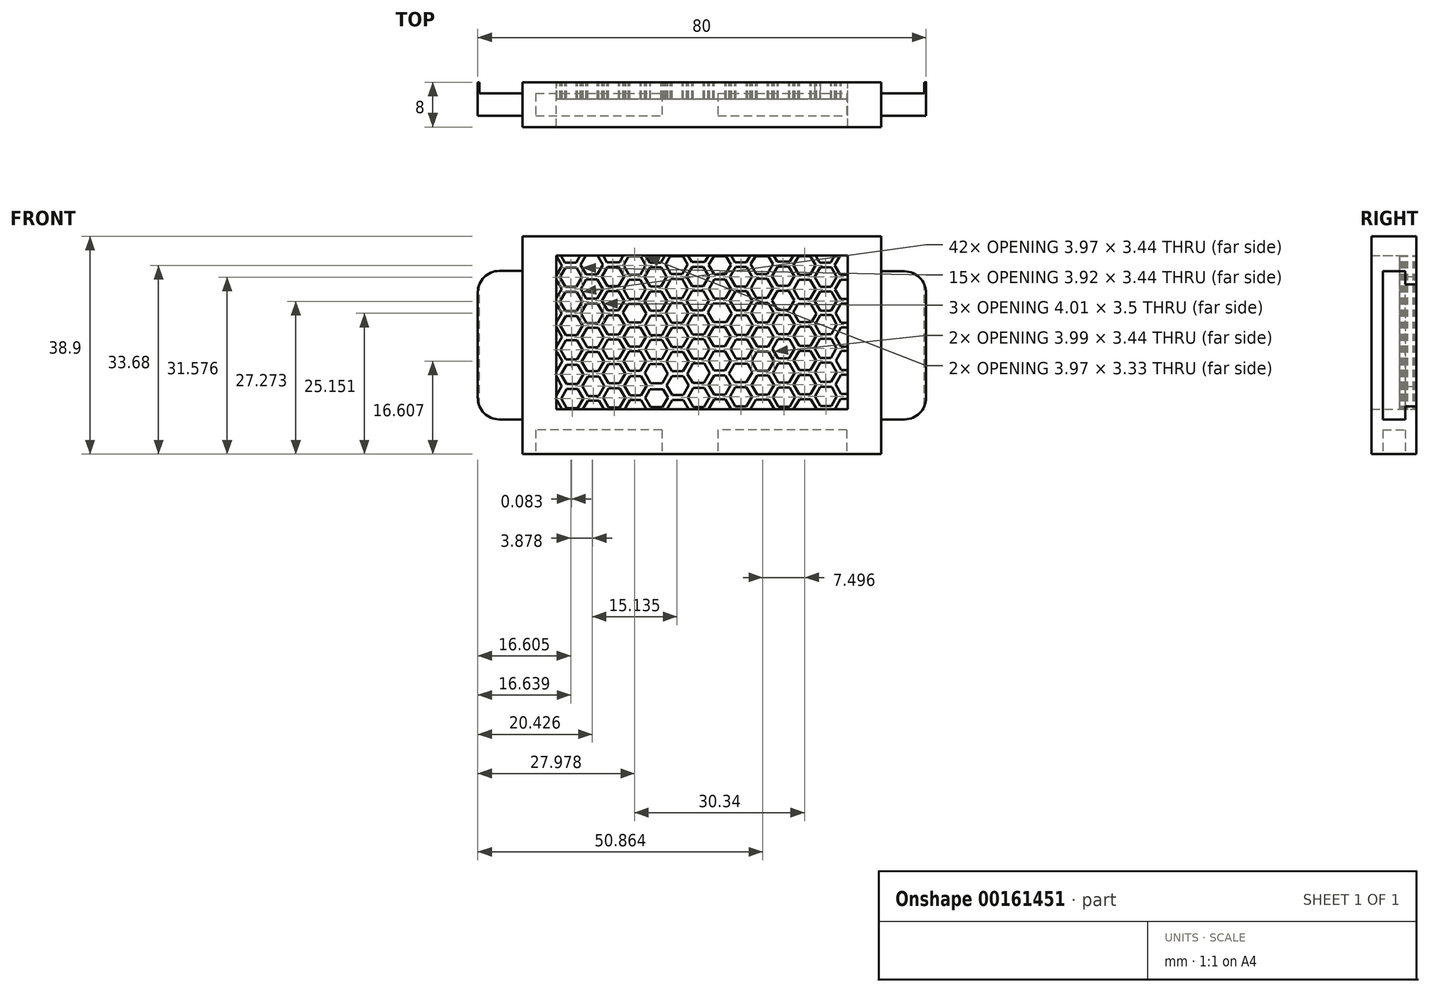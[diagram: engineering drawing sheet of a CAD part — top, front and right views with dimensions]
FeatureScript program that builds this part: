
annotation { "Feature Type Name" : "Feature", "Feature Type Description" : "" }
export const myFeature = defineFeature(function(context is Context, id is Id, definition is map)
    precondition{}
    {
        {
            var Q0;
            Q0=qCreatedBy(makeId("Front.planeOp"),FACE);
            var sketch = newSketch(context, id + "F0", { "sketchPlane" : qUnion([Q0])});
            skLineSegment(sketch, "E0.top", {"start": v(-77.72, 0.67) * mm, "end": v(-71.72, 0.67) * mm});
            skLineSegment(sketch, "E0.left", {"start": v(-77.72, 39.57) * mm, "end": v(-77.72, 0.67) * mm});
            skLineSegment(sketch, "E0.right", {"start": v(-13.72, 39.57) * mm, "end": v(-13.72, 0.67) * mm});
            skLineSegment(sketch, "E1.left", {"start": v(-77.72, 0.67) * mm, "end": v(-77.72, 15.56) * mm});
            skLineSegment(sketch, "E1.right", {"start": v(-85.72, 10.7) * mm, "end": v(-85.72, 29.54) * mm});
            skLineSegment(sketch, "E2.top", {"start": v(-77.72, 6.87) * mm, "end": v(-81.89, 6.87) * mm});
            skLineSegment(sketch, "E2.left", {"start": v(-77.72, 0.67) * mm, "end": v(-77.72, 6.87) * mm});
            skLineSegment(sketch, "E3.top", {"start": v(-81.89, 33.37) * mm, "end": v(-77.72, 33.37) * mm});
            skLineSegment(sketch, "E3.right", {"start": v(-77.72, 33.37) * mm, "end": v(-77.72, 15.56) * mm});
            skArc(sketch, "E4.filletArc", {"start": v(-81.89, 33.37) * mm, "mid": v(-84.6, 32.25) * mm, "end": v(-85.72, 29.54) * mm});
            skPoint(sketch, "E5.visualSharp", {"position": v(-85.72, 6.87) * mm});
            skArc(sketch, "E5.filletArc", {"start": v(-85.72, 10.7) * mm, "mid": v(-84.6, 8) * mm, "end": v(-81.89, 6.87) * mm});
            skLineSegment(sketch, "E6.right", {"start": v(-71.72, 36.1) * mm, "end": v(-71.72, 32.73) * mm});
            skLineSegment(sketch, "E7.top", {"start": v(-13.72, 0.67) * mm, "end": v(-19.72, 0.67) * mm});
            skLineSegment(sketch, "E7.right", {"start": v(-19.72, 36.1) * mm, "end": v(-19.72, 8.67) * mm});
            skLineSegment(sketch, "E8.left", {"start": v(-77.72, 8.67) * mm, "end": v(-77.72, 0.67) * mm});
            skLineSegment(sketch, "E8.right", {"start": v(-13.72, 6.87) * mm, "end": v(-13.72, 0.67) * mm});
            skLineSegment(sketch, "E9.bottom", {"start": v(-36.17, 36.01) * mm, "end": v(-33.87, 36.01) * mm});
            skLineSegment(sketch, "E10.trimOffspring", {"start": v(-43.6, 36.01) * mm, "end": v(-41.43, 36.01) * mm});
            skLineSegment(sketch, "E11.trimOffspring", {"start": v(-28.45, 36.01) * mm, "end": v(-26.35, 36.01) * mm});
            skLineSegment(sketch, "E12", {"start": v(-85.42, 9.22) * mm, "end": v(-85.42, 31.03) * mm});
            skLineSegment(sketch, "E13.0", {"start": v(-64.38, 28.45) * mm, "end": v(-66.36, 28.45) * mm});
            skLineSegment(sketch, "E13.1", {"start": v(-66.36, 28.45) * mm, "end": v(-67.36, 30.17) * mm});
            skLineSegment(sketch, "E13.2", {"start": v(-67.36, 30.17) * mm, "end": v(-66.36, 31.89) * mm});
            skLineSegment(sketch, "E13.3", {"start": v(-66.36, 31.89) * mm, "end": v(-64.38, 31.89) * mm});
            skLineSegment(sketch, "E13.4", {"start": v(-64.38, 31.89) * mm, "end": v(-63.39, 30.17) * mm});
            skLineSegment(sketch, "E13.5", {"start": v(-63.39, 30.17) * mm, "end": v(-64.38, 28.45) * mm});
            skLineSegment(sketch, "E14", {"start": v(-67.15, 32.27) * mm, "end": v(-68.16, 30.53) * mm});
            skLineSegment(sketch, "E15", {"start": v(-66.3, 27.57) * mm, "end": v(-64.3, 27.57) * mm});
            skLineSegment(sketch, "E16.0", {"start": v(-64.39, 32.75) * mm, "end": v(-66.37, 32.75) * mm});
            skLineSegment(sketch, "E16.1", {"start": v(-66.37, 32.75) * mm, "end": v(-67.36, 34.47) * mm});
            skLineSegment(sketch, "E16.2", {"start": v(-67.36, 34.47) * mm, "end": v(-66.43, 36.1) * mm});
            skLineSegment(sketch, "E16.5", {"start": v(-63.4, 34.47) * mm, "end": v(-64.39, 32.75) * mm});
            skLineSegment(sketch, "E17", {"start": v(-67.44, 36.1) * mm, "end": v(-68.17, 34.83) * mm});
            skLineSegment(sketch, "E18.0", {"start": v(-60.6, 26.33) * mm, "end": v(-62.58, 26.33) * mm});
            skLineSegment(sketch, "E18.1", {"start": v(-62.58, 26.33) * mm, "end": v(-63.57, 28.05) * mm});
            skLineSegment(sketch, "E18.2", {"start": v(-63.57, 28.05) * mm, "end": v(-62.58, 29.77) * mm});
            skLineSegment(sketch, "E18.3", {"start": v(-62.58, 29.77) * mm, "end": v(-60.6, 29.77) * mm});
            skLineSegment(sketch, "E18.4", {"start": v(-60.6, 29.77) * mm, "end": v(-59.6, 28.05) * mm});
            skLineSegment(sketch, "E18.5", {"start": v(-59.6, 28.05) * mm, "end": v(-60.6, 26.33) * mm});
            skLineSegment(sketch, "E19", {"start": v(-64.3, 27.57) * mm, "end": v(-63.29, 25.81) * mm});
            skLineSegment(sketch, "E20", {"start": v(-58.91, 27.5) * mm, "end": v(-59.8, 25.94) * mm});
            skLineSegment(sketch, "E21.0", {"start": v(-60.6, 30.63) * mm, "end": v(-62.59, 30.63) * mm});
            skLineSegment(sketch, "E21.1", {"start": v(-62.59, 30.63) * mm, "end": v(-63.58, 32.35) * mm});
            skLineSegment(sketch, "E21.2", {"start": v(-63.58, 32.35) * mm, "end": v(-62.59, 34.07) * mm});
            skLineSegment(sketch, "E21.3", {"start": v(-62.59, 34.07) * mm, "end": v(-60.6, 34.07) * mm});
            skLineSegment(sketch, "E21.4", {"start": v(-60.6, 34.07) * mm, "end": v(-59.6, 32.35) * mm});
            skLineSegment(sketch, "E21.5", {"start": v(-59.6, 32.35) * mm, "end": v(-60.6, 30.63) * mm});
            skLineSegment(sketch, "E22", {"start": v(-60.43, 34.94) * mm, "end": v(-62.66, 34.94) * mm});
            skLineSegment(sketch, "E23.0", {"start": v(-68.09, 26.22) * mm, "end": v(-70.07, 26.22) * mm});
            skLineSegment(sketch, "E23.1", {"start": v(-70.07, 26.22) * mm, "end": v(-71.07, 27.94) * mm});
            skLineSegment(sketch, "E23.2", {"start": v(-71.07, 27.94) * mm, "end": v(-70.07, 29.66) * mm});
            skLineSegment(sketch, "E23.3", {"start": v(-70.07, 29.66) * mm, "end": v(-68.1, 29.66) * mm});
            skLineSegment(sketch, "E23.4", {"start": v(-68.1, 29.66) * mm, "end": v(-67.1, 27.94) * mm});
            skLineSegment(sketch, "E23.5", {"start": v(-67.1, 27.94) * mm, "end": v(-68.09, 26.22) * mm});
            skLineSegment(sketch, "E24", {"start": v(-66.3, 27.57) * mm, "end": v(-67.3, 25.83) * mm});
            skLineSegment(sketch, "E25.0", {"start": v(-68.16, 30.53) * mm, "end": v(-70.08, 30.53) * mm});
            skLineSegment(sketch, "E25.1", {"start": v(-70.08, 30.53) * mm, "end": v(-71.07, 32.25) * mm});
            skLineSegment(sketch, "E25.2", {"start": v(-71.07, 32.25) * mm, "end": v(-70.08, 33.96) * mm});
            skLineSegment(sketch, "E25.3", {"start": v(-70.08, 33.96) * mm, "end": v(-68.1, 33.96) * mm});
            skLineSegment(sketch, "E25.4", {"start": v(-68.1, 33.96) * mm, "end": v(-67.15, 32.27) * mm});
            skLineSegment(sketch, "E26", {"start": v(-68.17, 34.83) * mm, "end": v(-70.16, 34.83) * mm});
            skLineSegment(sketch, "E27.0", {"start": v(-60.5, 17.7) * mm, "end": v(-62.49, 17.7) * mm});
            skLineSegment(sketch, "E27.1", {"start": v(-62.49, 17.7) * mm, "end": v(-63.48, 19.41) * mm});
            skLineSegment(sketch, "E27.2", {"start": v(-63.48, 19.41) * mm, "end": v(-62.49, 21.13) * mm});
            skLineSegment(sketch, "E27.3", {"start": v(-62.49, 21.13) * mm, "end": v(-60.5, 21.13) * mm});
            skLineSegment(sketch, "E27.4", {"start": v(-60.5, 21.13) * mm, "end": v(-59.5, 19.41) * mm});
            skLineSegment(sketch, "E27.5", {"start": v(-59.5, 19.41) * mm, "end": v(-60.5, 17.7) * mm});
            skLineSegment(sketch, "E28", {"start": v(-63.28, 21.51) * mm, "end": v(-64.28, 19.77) * mm});
            skLineSegment(sketch, "E29.0", {"start": v(-60.51, 22) * mm, "end": v(-62.5, 22) * mm});
            skLineSegment(sketch, "E29.1", {"start": v(-62.5, 22) * mm, "end": v(-63.49, 23.71) * mm});
            skLineSegment(sketch, "E29.2", {"start": v(-63.49, 23.71) * mm, "end": v(-62.5, 25.43) * mm});
            skLineSegment(sketch, "E29.3", {"start": v(-62.5, 25.43) * mm, "end": v(-60.51, 25.43) * mm});
            skLineSegment(sketch, "E29.4", {"start": v(-60.51, 25.43) * mm, "end": v(-59.52, 23.71) * mm});
            skLineSegment(sketch, "E29.5", {"start": v(-59.52, 23.71) * mm, "end": v(-60.51, 22) * mm});
            skLineSegment(sketch, "E30", {"start": v(-63.29, 25.81) * mm, "end": v(-64.3, 24.07) * mm});
            skLineSegment(sketch, "E31", {"start": v(-59.8, 25.94) * mm, "end": v(-58.79, 24.18) * mm});
            skLineSegment(sketch, "E32.0", {"start": v(-56.72, 15.57) * mm, "end": v(-58.7, 15.57) * mm});
            skLineSegment(sketch, "E32.1", {"start": v(-58.7, 15.57) * mm, "end": v(-59.7, 17.29) * mm});
            skLineSegment(sketch, "E32.2", {"start": v(-59.7, 17.29) * mm, "end": v(-58.7, 19) * mm});
            skLineSegment(sketch, "E32.3", {"start": v(-58.7, 19) * mm, "end": v(-56.72, 19) * mm});
            skLineSegment(sketch, "E32.4", {"start": v(-56.72, 19) * mm, "end": v(-55.72, 17.29) * mm});
            skLineSegment(sketch, "E32.5", {"start": v(-55.72, 17.29) * mm, "end": v(-56.72, 15.57) * mm});
            skLineSegment(sketch, "E33", {"start": v(-60.38, 16.73) * mm, "end": v(-59.39, 15.01) * mm});
            skLineSegment(sketch, "E34", {"start": v(-55.03, 16.74) * mm, "end": v(-55.92, 15.18) * mm});
            skLineSegment(sketch, "E35.0", {"start": v(-56.72, 19.87) * mm, "end": v(-58.7, 19.87) * mm});
            skLineSegment(sketch, "E35.1", {"start": v(-58.7, 19.87) * mm, "end": v(-59.7, 21.6) * mm});
            skLineSegment(sketch, "E35.2", {"start": v(-59.7, 21.6) * mm, "end": v(-58.7, 23.31) * mm});
            skLineSegment(sketch, "E35.3", {"start": v(-58.7, 23.31) * mm, "end": v(-56.72, 23.31) * mm});
            skLineSegment(sketch, "E35.4", {"start": v(-56.72, 23.31) * mm, "end": v(-55.73, 21.6) * mm});
            skLineSegment(sketch, "E35.5", {"start": v(-55.73, 21.6) * mm, "end": v(-56.72, 19.87) * mm});
            skLineSegment(sketch, "E36", {"start": v(-56.55, 24.18) * mm, "end": v(-58.79, 24.18) * mm});
            skLineSegment(sketch, "E37", {"start": v(-58.7, 19) * mm, "end": v(-56.7, 19) * mm});
            skLineSegment(sketch, "E38.0", {"start": v(-68, 17.59) * mm, "end": v(-69.98, 17.59) * mm});
            skLineSegment(sketch, "E38.1", {"start": v(-69.98, 17.59) * mm, "end": v(-70.97, 19.3) * mm});
            skLineSegment(sketch, "E38.2", {"start": v(-70.97, 19.3) * mm, "end": v(-69.98, 21.02) * mm});
            skLineSegment(sketch, "E38.3", {"start": v(-69.98, 21.02) * mm, "end": v(-68, 21.02) * mm});
            skLineSegment(sketch, "E38.4", {"start": v(-68, 21.02) * mm, "end": v(-67, 19.3) * mm});
            skLineSegment(sketch, "E38.5", {"start": v(-67, 19.3) * mm, "end": v(-68, 17.59) * mm});
            skLineSegment(sketch, "E39.0", {"start": v(-68, 21.89) * mm, "end": v(-70, 21.89) * mm});
            skLineSegment(sketch, "E39.1", {"start": v(-70, 21.89) * mm, "end": v(-70.98, 23.6) * mm});
            skLineSegment(sketch, "E39.2", {"start": v(-70.98, 23.6) * mm, "end": v(-70, 25.33) * mm});
            skLineSegment(sketch, "E39.3", {"start": v(-70, 25.33) * mm, "end": v(-68, 25.33) * mm});
            skLineSegment(sketch, "E39.4", {"start": v(-68, 25.33) * mm, "end": v(-67.01, 23.6) * mm});
            skLineSegment(sketch, "E39.5", {"start": v(-67.01, 23.6) * mm, "end": v(-68, 21.89) * mm});
            skLineSegment(sketch, "E40", {"start": v(-67.3, 25.83) * mm, "end": v(-66.28, 24.07) * mm});
            skLineSegment(sketch, "E41.0", {"start": v(-64.21, 15.46) * mm, "end": v(-66.2, 15.46) * mm});
            skLineSegment(sketch, "E41.1", {"start": v(-66.2, 15.46) * mm, "end": v(-67.19, 17.18) * mm});
            skLineSegment(sketch, "E41.2", {"start": v(-67.19, 17.18) * mm, "end": v(-66.2, 18.9) * mm});
            skLineSegment(sketch, "E41.3", {"start": v(-66.2, 18.9) * mm, "end": v(-64.21, 18.9) * mm});
            skLineSegment(sketch, "E41.4", {"start": v(-64.21, 18.9) * mm, "end": v(-63.22, 17.18) * mm});
            skLineSegment(sketch, "E41.5", {"start": v(-63.22, 17.18) * mm, "end": v(-64.21, 15.46) * mm});
            skLineSegment(sketch, "E42.0", {"start": v(-64.28, 19.77) * mm, "end": v(-66.2, 19.77) * mm});
            skLineSegment(sketch, "E42.1", {"start": v(-66.2, 19.77) * mm, "end": v(-67.2, 21.49) * mm});
            skLineSegment(sketch, "E42.2", {"start": v(-67.2, 21.49) * mm, "end": v(-66.2, 23.2) * mm});
            skLineSegment(sketch, "E42.3", {"start": v(-66.2, 23.2) * mm, "end": v(-64.22, 23.2) * mm});
            skLineSegment(sketch, "E42.4", {"start": v(-64.22, 23.2) * mm, "end": v(-63.28, 21.51) * mm});
            skLineSegment(sketch, "E43", {"start": v(-64.3, 24.07) * mm, "end": v(-66.28, 24.07) * mm});
            skLineSegment(sketch, "E44.0", {"start": v(-49.24, 28.49) * mm, "end": v(-51.23, 28.49) * mm});
            skLineSegment(sketch, "E44.1", {"start": v(-51.23, 28.49) * mm, "end": v(-52.22, 30.2) * mm});
            skLineSegment(sketch, "E44.2", {"start": v(-52.22, 30.2) * mm, "end": v(-51.23, 31.93) * mm});
            skLineSegment(sketch, "E44.3", {"start": v(-51.23, 31.93) * mm, "end": v(-49.25, 31.93) * mm});
            skLineSegment(sketch, "E44.4", {"start": v(-49.25, 31.93) * mm, "end": v(-48.25, 30.2) * mm});
            skLineSegment(sketch, "E44.5", {"start": v(-48.25, 30.2) * mm, "end": v(-49.24, 28.49) * mm});
            skLineSegment(sketch, "E45", {"start": v(-52.02, 32.31) * mm, "end": v(-53.03, 30.57) * mm});
            skLineSegment(sketch, "E46", {"start": v(-51.17, 27.6) * mm, "end": v(-49.17, 27.6) * mm});
            skLineSegment(sketch, "E47.0", {"start": v(-49.25, 32.8) * mm, "end": v(-51.24, 32.8) * mm});
            skLineSegment(sketch, "E47.1", {"start": v(-51.24, 32.8) * mm, "end": v(-52.23, 34.51) * mm});
            skLineSegment(sketch, "E47.2", {"start": v(-52.23, 34.51) * mm, "end": v(-51.36, 36.01) * mm});
            skLineSegment(sketch, "E47.4", {"start": v(-49.13, 36.01) * mm, "end": v(-48.26, 34.51) * mm});
            skLineSegment(sketch, "E47.5", {"start": v(-48.26, 34.51) * mm, "end": v(-49.25, 32.8) * mm});
            skLineSegment(sketch, "E48", {"start": v(-52.38, 36.01) * mm, "end": v(-53.04, 34.87) * mm});
            skLineSegment(sketch, "E49", {"start": v(-48.13, 36.01) * mm, "end": v(-47.53, 34.97) * mm});
            skLineSegment(sketch, "E50.0", {"start": v(-45.46, 26.37) * mm, "end": v(-47.44, 26.37) * mm});
            skLineSegment(sketch, "E50.1", {"start": v(-47.44, 26.37) * mm, "end": v(-48.43, 28.09) * mm});
            skLineSegment(sketch, "E50.2", {"start": v(-48.43, 28.09) * mm, "end": v(-47.44, 29.8) * mm});
            skLineSegment(sketch, "E50.3", {"start": v(-47.44, 29.8) * mm, "end": v(-45.46, 29.8) * mm});
            skLineSegment(sketch, "E50.4", {"start": v(-45.46, 29.8) * mm, "end": v(-44.47, 28.09) * mm});
            skLineSegment(sketch, "E50.5", {"start": v(-44.47, 28.09) * mm, "end": v(-45.46, 26.37) * mm});
            skLineSegment(sketch, "E51", {"start": v(-49.17, 27.6) * mm, "end": v(-48.15, 25.85) * mm});
            skLineSegment(sketch, "E52", {"start": v(-43.77, 27.56) * mm, "end": v(-44.67, 25.98) * mm});
            skLineSegment(sketch, "E53.0", {"start": v(-45.47, 30.67) * mm, "end": v(-47.45, 30.67) * mm});
            skLineSegment(sketch, "E53.1", {"start": v(-47.45, 30.67) * mm, "end": v(-48.44, 32.4) * mm});
            skLineSegment(sketch, "E53.2", {"start": v(-48.44, 32.4) * mm, "end": v(-47.45, 34.1) * mm});
            skLineSegment(sketch, "E53.3", {"start": v(-47.45, 34.1) * mm, "end": v(-45.47, 34.1) * mm});
            skLineSegment(sketch, "E53.4", {"start": v(-45.47, 34.1) * mm, "end": v(-44.47, 32.4) * mm});
            skLineSegment(sketch, "E53.5", {"start": v(-44.47, 32.4) * mm, "end": v(-45.47, 30.67) * mm});
            skLineSegment(sketch, "E54", {"start": v(-45.22, 34.97) * mm, "end": v(-47.53, 34.97) * mm});
            skLineSegment(sketch, "E55", {"start": v(-47.45, 29.8) * mm, "end": v(-45.45, 29.8) * mm});
            skLineSegment(sketch, "E56.0", {"start": v(-56.74, 28.38) * mm, "end": v(-58.73, 28.38) * mm});
            skLineSegment(sketch, "E56.1", {"start": v(-58.73, 28.38) * mm, "end": v(-59.72, 30.1) * mm});
            skLineSegment(sketch, "E56.2", {"start": v(-59.72, 30.1) * mm, "end": v(-58.73, 31.82) * mm});
            skLineSegment(sketch, "E56.3", {"start": v(-58.73, 31.82) * mm, "end": v(-56.74, 31.82) * mm});
            skLineSegment(sketch, "E56.4", {"start": v(-56.74, 31.82) * mm, "end": v(-55.75, 30.1) * mm});
            skLineSegment(sketch, "E56.5", {"start": v(-55.75, 30.1) * mm, "end": v(-56.74, 28.38) * mm});
            skLineSegment(sketch, "E57", {"start": v(-58.91, 27.5) * mm, "end": v(-56.67, 27.5) * mm});
            skLineSegment(sketch, "E58.0", {"start": v(-56.75, 32.69) * mm, "end": v(-58.73, 32.69) * mm});
            skLineSegment(sketch, "E58.1", {"start": v(-58.73, 32.69) * mm, "end": v(-59.73, 34.4) * mm});
            skLineSegment(sketch, "E58.2", {"start": v(-59.73, 34.4) * mm, "end": v(-58.8, 36.01) * mm});
            skLineSegment(sketch, "E58.4", {"start": v(-56.69, 36.01) * mm, "end": v(-55.76, 34.4) * mm});
            skLineSegment(sketch, "E58.5", {"start": v(-55.76, 34.4) * mm, "end": v(-56.75, 32.69) * mm});
            skLineSegment(sketch, "E59", {"start": v(-59.81, 36.01) * mm, "end": v(-60.43, 34.94) * mm});
            skLineSegment(sketch, "E60", {"start": v(-55.69, 36.01) * mm, "end": v(-55.02, 34.87) * mm});
            skLineSegment(sketch, "E61.0", {"start": v(-52.95, 26.26) * mm, "end": v(-54.94, 26.26) * mm});
            skLineSegment(sketch, "E61.1", {"start": v(-54.94, 26.26) * mm, "end": v(-55.93, 27.98) * mm});
            skLineSegment(sketch, "E61.2", {"start": v(-55.93, 27.98) * mm, "end": v(-54.94, 29.7) * mm});
            skLineSegment(sketch, "E61.3", {"start": v(-54.94, 29.7) * mm, "end": v(-52.96, 29.7) * mm});
            skLineSegment(sketch, "E61.4", {"start": v(-52.96, 29.7) * mm, "end": v(-51.96, 27.98) * mm});
            skLineSegment(sketch, "E61.5", {"start": v(-51.96, 27.98) * mm, "end": v(-52.95, 26.26) * mm});
            skLineSegment(sketch, "E62", {"start": v(-56.67, 27.5) * mm, "end": v(-55.65, 25.74) * mm});
            skLineSegment(sketch, "E63", {"start": v(-51.17, 27.6) * mm, "end": v(-52.16, 25.87) * mm});
            skLineSegment(sketch, "E64.0", {"start": v(-53.03, 30.57) * mm, "end": v(-54.95, 30.57) * mm});
            skLineSegment(sketch, "E64.1", {"start": v(-54.95, 30.57) * mm, "end": v(-55.94, 32.28) * mm});
            skLineSegment(sketch, "E64.2", {"start": v(-55.94, 32.28) * mm, "end": v(-54.95, 34) * mm});
            skLineSegment(sketch, "E64.3", {"start": v(-54.95, 34) * mm, "end": v(-52.96, 34) * mm});
            skLineSegment(sketch, "E64.4", {"start": v(-52.96, 34) * mm, "end": v(-52.02, 32.31) * mm});
            skLineSegment(sketch, "E65", {"start": v(-53.04, 34.87) * mm, "end": v(-55.02, 34.87) * mm});
            skLineSegment(sketch, "E66", {"start": v(-54.95, 29.69) * mm, "end": v(-52.95, 29.69) * mm});
            skLineSegment(sketch, "E67.0", {"start": v(-45.37, 17.73) * mm, "end": v(-47.35, 17.73) * mm});
            skLineSegment(sketch, "E67.1", {"start": v(-47.35, 17.73) * mm, "end": v(-48.34, 19.45) * mm});
            skLineSegment(sketch, "E67.2", {"start": v(-48.34, 19.45) * mm, "end": v(-47.35, 21.17) * mm});
            skLineSegment(sketch, "E67.3", {"start": v(-47.35, 21.17) * mm, "end": v(-45.37, 21.17) * mm});
            skLineSegment(sketch, "E67.4", {"start": v(-45.37, 21.17) * mm, "end": v(-44.37, 19.45) * mm});
            skLineSegment(sketch, "E67.5", {"start": v(-44.37, 19.45) * mm, "end": v(-45.37, 17.73) * mm});
            skLineSegment(sketch, "E68", {"start": v(-48.14, 21.55) * mm, "end": v(-49.15, 19.8) * mm});
            skLineSegment(sketch, "E69", {"start": v(-47.3, 16.85) * mm, "end": v(-45.3, 16.85) * mm});
            skLineSegment(sketch, "E70.0", {"start": v(-45.38, 22.03) * mm, "end": v(-47.36, 22.03) * mm});
            skLineSegment(sketch, "E70.1", {"start": v(-47.36, 22.03) * mm, "end": v(-48.35, 23.75) * mm});
            skLineSegment(sketch, "E70.2", {"start": v(-48.35, 23.75) * mm, "end": v(-47.36, 25.47) * mm});
            skLineSegment(sketch, "E70.3", {"start": v(-47.36, 25.47) * mm, "end": v(-45.38, 25.47) * mm});
            skLineSegment(sketch, "E70.4", {"start": v(-45.38, 25.47) * mm, "end": v(-44.38, 23.75) * mm});
            skLineSegment(sketch, "E70.5", {"start": v(-44.38, 23.75) * mm, "end": v(-45.38, 22.03) * mm});
            skLineSegment(sketch, "E71", {"start": v(-48.15, 25.85) * mm, "end": v(-49.16, 24.1) * mm});
            skLineSegment(sketch, "E72", {"start": v(-44.67, 25.98) * mm, "end": v(-43.65, 24.22) * mm});
            skLineSegment(sketch, "E73.0", {"start": v(-41.58, 15.6) * mm, "end": v(-43.56, 15.6) * mm});
            skLineSegment(sketch, "E73.1", {"start": v(-43.56, 15.6) * mm, "end": v(-44.56, 17.33) * mm});
            skLineSegment(sketch, "E73.2", {"start": v(-44.56, 17.33) * mm, "end": v(-43.57, 19.05) * mm});
            skLineSegment(sketch, "E73.3", {"start": v(-43.57, 19.05) * mm, "end": v(-41.58, 19.05) * mm});
            skLineSegment(sketch, "E73.4", {"start": v(-41.58, 19.05) * mm, "end": v(-40.59, 17.33) * mm});
            skLineSegment(sketch, "E73.5", {"start": v(-40.59, 17.33) * mm, "end": v(-41.58, 15.6) * mm});
            skLineSegment(sketch, "E74", {"start": v(-45.3, 16.85) * mm, "end": v(-44.32, 15.16) * mm});
            skLineSegment(sketch, "E75", {"start": v(-39.89, 16.8) * mm, "end": v(-40.88, 15.05) * mm});
            skLineSegment(sketch, "E76.0", {"start": v(-41.59, 19.91) * mm, "end": v(-43.57, 19.91) * mm});
            skLineSegment(sketch, "E76.1", {"start": v(-43.57, 19.91) * mm, "end": v(-44.57, 21.63) * mm});
            skLineSegment(sketch, "E76.2", {"start": v(-44.57, 21.63) * mm, "end": v(-43.57, 23.35) * mm});
            skLineSegment(sketch, "E76.3", {"start": v(-43.57, 23.35) * mm, "end": v(-41.59, 23.35) * mm});
            skLineSegment(sketch, "E76.4", {"start": v(-41.59, 23.35) * mm, "end": v(-40.6, 21.63) * mm});
            skLineSegment(sketch, "E76.5", {"start": v(-40.6, 21.63) * mm, "end": v(-41.59, 19.91) * mm});
            skLineSegment(sketch, "E77", {"start": v(-41.34, 24.22) * mm, "end": v(-43.65, 24.22) * mm});
            skLineSegment(sketch, "E78.0", {"start": v(-52.86, 17.62) * mm, "end": v(-54.85, 17.62) * mm});
            skLineSegment(sketch, "E78.1", {"start": v(-54.85, 17.62) * mm, "end": v(-55.84, 19.34) * mm});
            skLineSegment(sketch, "E78.2", {"start": v(-55.84, 19.34) * mm, "end": v(-54.85, 21.06) * mm});
            skLineSegment(sketch, "E78.3", {"start": v(-54.85, 21.06) * mm, "end": v(-52.86, 21.06) * mm});
            skLineSegment(sketch, "E78.4", {"start": v(-52.86, 21.06) * mm, "end": v(-51.87, 19.34) * mm});
            skLineSegment(sketch, "E78.5", {"start": v(-51.87, 19.34) * mm, "end": v(-52.86, 17.62) * mm});
            skLineSegment(sketch, "E79", {"start": v(-55.03, 16.74) * mm, "end": v(-52.79, 16.74) * mm});
            skLineSegment(sketch, "E80.0", {"start": v(-52.87, 21.93) * mm, "end": v(-54.86, 21.93) * mm});
            skLineSegment(sketch, "E80.1", {"start": v(-54.86, 21.93) * mm, "end": v(-55.85, 23.64) * mm});
            skLineSegment(sketch, "E80.2", {"start": v(-55.85, 23.64) * mm, "end": v(-54.86, 25.36) * mm});
            skLineSegment(sketch, "E80.3", {"start": v(-54.86, 25.36) * mm, "end": v(-52.87, 25.36) * mm});
            skLineSegment(sketch, "E80.4", {"start": v(-52.87, 25.36) * mm, "end": v(-51.88, 23.64) * mm});
            skLineSegment(sketch, "E80.5", {"start": v(-51.88, 23.64) * mm, "end": v(-52.87, 21.93) * mm});
            skLineSegment(sketch, "E81", {"start": v(-55.65, 25.74) * mm, "end": v(-56.55, 24.18) * mm});
            skLineSegment(sketch, "E82", {"start": v(-52.16, 25.87) * mm, "end": v(-51.15, 24.1) * mm});
            skLineSegment(sketch, "E83.0", {"start": v(-49.08, 15.5) * mm, "end": v(-51.06, 15.5) * mm});
            skLineSegment(sketch, "E83.1", {"start": v(-51.06, 15.5) * mm, "end": v(-52.05, 17.22) * mm});
            skLineSegment(sketch, "E83.2", {"start": v(-52.05, 17.22) * mm, "end": v(-51.06, 18.94) * mm});
            skLineSegment(sketch, "E83.3", {"start": v(-51.06, 18.94) * mm, "end": v(-49.08, 18.94) * mm});
            skLineSegment(sketch, "E83.4", {"start": v(-49.08, 18.94) * mm, "end": v(-48.08, 17.22) * mm});
            skLineSegment(sketch, "E83.5", {"start": v(-48.08, 17.22) * mm, "end": v(-49.08, 15.5) * mm});
            skLineSegment(sketch, "E84", {"start": v(-52.79, 16.74) * mm, "end": v(-51.81, 15.05) * mm});
            skLineSegment(sketch, "E85", {"start": v(-51.05, 14.62) * mm, "end": v(-49.04, 14.62) * mm});
            skLineSegment(sketch, "E86", {"start": v(-47.3, 16.85) * mm, "end": v(-48.36, 14.99) * mm});
            skLineSegment(sketch, "E87.0", {"start": v(-49.15, 19.8) * mm, "end": v(-51.07, 19.8) * mm});
            skLineSegment(sketch, "E87.1", {"start": v(-51.07, 19.8) * mm, "end": v(-52.06, 21.52) * mm});
            skLineSegment(sketch, "E87.2", {"start": v(-52.06, 21.52) * mm, "end": v(-51.07, 23.24) * mm});
            skLineSegment(sketch, "E87.3", {"start": v(-51.07, 23.24) * mm, "end": v(-49.09, 23.24) * mm});
            skLineSegment(sketch, "E87.4", {"start": v(-49.09, 23.24) * mm, "end": v(-48.14, 21.55) * mm});
            skLineSegment(sketch, "E88", {"start": v(-49.16, 24.1) * mm, "end": v(-51.15, 24.1) * mm});
            skLineSegment(sketch, "E89.0", {"start": v(-60.37, 9) * mm, "end": v(-62.36, 9) * mm});
            skLineSegment(sketch, "E89.1", {"start": v(-62.36, 9) * mm, "end": v(-63.35, 10.71) * mm});
            skLineSegment(sketch, "E89.2", {"start": v(-63.35, 10.71) * mm, "end": v(-62.36, 12.43) * mm});
            skLineSegment(sketch, "E89.3", {"start": v(-62.36, 12.43) * mm, "end": v(-60.37, 12.43) * mm});
            skLineSegment(sketch, "E89.4", {"start": v(-60.37, 12.43) * mm, "end": v(-59.38, 10.71) * mm});
            skLineSegment(sketch, "E89.5", {"start": v(-59.38, 10.71) * mm, "end": v(-60.37, 9) * mm});
            skLineSegment(sketch, "E90", {"start": v(-63.15, 12.82) * mm, "end": v(-64.16, 11.07) * mm});
            skLineSegment(sketch, "E91.0", {"start": v(-60.38, 13.3) * mm, "end": v(-62.37, 13.3) * mm});
            skLineSegment(sketch, "E91.1", {"start": v(-62.37, 13.3) * mm, "end": v(-63.36, 15.01) * mm});
            skLineSegment(sketch, "E91.2", {"start": v(-63.36, 15.01) * mm, "end": v(-62.37, 16.73) * mm});
            skLineSegment(sketch, "E91.3", {"start": v(-62.37, 16.73) * mm, "end": v(-60.38, 16.73) * mm});
            skLineSegment(sketch, "E91.5", {"start": v(-59.39, 15.01) * mm, "end": v(-60.38, 13.3) * mm});
            skLineSegment(sketch, "E92.2", {"start": v(-59.24, 9.15) * mm, "end": v(-58.57, 10.3) * mm});
            skLineSegment(sketch, "E92.3", {"start": v(-58.57, 10.3) * mm, "end": v(-56.59, 10.3) * mm});
            skLineSegment(sketch, "E92.4", {"start": v(-56.59, 10.3) * mm, "end": v(-55.67, 8.67) * mm});
            skLineSegment(sketch, "E93", {"start": v(-55.83, 10.73) * mm, "end": v(-54.88, 9.04) * mm});
            skLineSegment(sketch, "E94.0", {"start": v(-56.6, 11.18) * mm, "end": v(-58.58, 11.18) * mm});
            skLineSegment(sketch, "E94.1", {"start": v(-58.58, 11.18) * mm, "end": v(-59.57, 12.9) * mm});
            skLineSegment(sketch, "E94.2", {"start": v(-59.57, 12.9) * mm, "end": v(-58.58, 14.61) * mm});
            skLineSegment(sketch, "E94.3", {"start": v(-58.58, 14.61) * mm, "end": v(-56.6, 14.61) * mm});
            skLineSegment(sketch, "E94.4", {"start": v(-56.6, 14.61) * mm, "end": v(-55.6, 12.9) * mm});
            skLineSegment(sketch, "E94.5", {"start": v(-55.6, 12.9) * mm, "end": v(-56.6, 11.18) * mm});
            skLineSegment(sketch, "E95", {"start": v(-55.92, 15.18) * mm, "end": v(-54.87, 13.35) * mm});
            skLineSegment(sketch, "E96", {"start": v(-54.98, 12.22) * mm, "end": v(-55.83, 10.73) * mm});
            skLineSegment(sketch, "E97.0", {"start": v(-67.87, 8.89) * mm, "end": v(-69.85, 8.89) * mm});
            skLineSegment(sketch, "E97.1", {"start": v(-69.85, 8.89) * mm, "end": v(-70.85, 10.6) * mm});
            skLineSegment(sketch, "E97.2", {"start": v(-70.85, 10.6) * mm, "end": v(-69.85, 12.32) * mm});
            skLineSegment(sketch, "E97.3", {"start": v(-69.85, 12.32) * mm, "end": v(-67.87, 12.32) * mm});
            skLineSegment(sketch, "E97.4", {"start": v(-67.87, 12.32) * mm, "end": v(-66.88, 10.6) * mm});
            skLineSegment(sketch, "E97.5", {"start": v(-66.88, 10.6) * mm, "end": v(-67.87, 8.89) * mm});
            skLineSegment(sketch, "E98.0", {"start": v(-67.88, 13.19) * mm, "end": v(-69.86, 13.19) * mm});
            skLineSegment(sketch, "E98.1", {"start": v(-69.86, 13.19) * mm, "end": v(-70.85, 14.9) * mm});
            skLineSegment(sketch, "E98.2", {"start": v(-70.85, 14.9) * mm, "end": v(-69.86, 16.63) * mm});
            skLineSegment(sketch, "E98.3", {"start": v(-69.86, 16.63) * mm, "end": v(-67.88, 16.63) * mm});
            skLineSegment(sketch, "E98.4", {"start": v(-67.88, 16.63) * mm, "end": v(-66.89, 14.9) * mm});
            skLineSegment(sketch, "E98.5", {"start": v(-66.89, 14.9) * mm, "end": v(-67.88, 13.19) * mm});
            skLineSegment(sketch, "E99", {"start": v(-69.86, 12.31) * mm, "end": v(-67.86, 12.31) * mm});
            skLineSegment(sketch, "E100.3", {"start": v(-66.07, 10.2) * mm, "end": v(-64.08, 10.2) * mm});
            skLineSegment(sketch, "E100.4", {"start": v(-64.08, 10.2) * mm, "end": v(-63.22, 8.7) * mm});
            skLineSegment(sketch, "E101.0", {"start": v(-64.16, 11.07) * mm, "end": v(-66.08, 11.07) * mm});
            skLineSegment(sketch, "E101.1", {"start": v(-66.08, 11.07) * mm, "end": v(-67.07, 12.79) * mm});
            skLineSegment(sketch, "E101.2", {"start": v(-67.07, 12.79) * mm, "end": v(-66.08, 14.5) * mm});
            skLineSegment(sketch, "E101.3", {"start": v(-66.08, 14.5) * mm, "end": v(-64.1, 14.5) * mm});
            skLineSegment(sketch, "E101.4", {"start": v(-64.1, 14.5) * mm, "end": v(-63.15, 12.82) * mm});
            skLineSegment(sketch, "E102.1", {"start": v(-44.5, 8.67) * mm, "end": v(-44.52, 8.73) * mm});
            skLineSegment(sketch, "E102.2", {"start": v(-44.52, 8.73) * mm, "end": v(-43.53, 10.45) * mm});
            skLineSegment(sketch, "E102.3", {"start": v(-43.53, 10.45) * mm, "end": v(-41.55, 10.45) * mm});
            skLineSegment(sketch, "E102.4", {"start": v(-41.55, 10.45) * mm, "end": v(-40.55, 8.73) * mm});
            skLineSegment(sketch, "E103", {"start": v(-44.32, 10.83) * mm, "end": v(-45.33, 9.09) * mm});
            skLineSegment(sketch, "E104.0", {"start": v(-41.56, 11.31) * mm, "end": v(-43.54, 11.31) * mm});
            skLineSegment(sketch, "E104.1", {"start": v(-43.54, 11.31) * mm, "end": v(-44.53, 13.03) * mm});
            skLineSegment(sketch, "E104.2", {"start": v(-44.53, 13.03) * mm, "end": v(-43.54, 14.75) * mm});
            skLineSegment(sketch, "E104.3", {"start": v(-43.54, 14.75) * mm, "end": v(-41.56, 14.75) * mm});
            skLineSegment(sketch, "E104.4", {"start": v(-41.56, 14.75) * mm, "end": v(-40.56, 13.03) * mm});
            skLineSegment(sketch, "E104.5", {"start": v(-40.56, 13.03) * mm, "end": v(-41.56, 11.31) * mm});
            skLineSegment(sketch, "E105.0", {"start": v(-37.77, 9.2) * mm, "end": v(-39.75, 9.2) * mm});
            skLineSegment(sketch, "E105.1", {"start": v(-39.75, 9.2) * mm, "end": v(-40.75, 10.91) * mm});
            skLineSegment(sketch, "E105.2", {"start": v(-40.75, 10.91) * mm, "end": v(-39.75, 12.63) * mm});
            skLineSegment(sketch, "E105.3", {"start": v(-39.75, 12.63) * mm, "end": v(-37.77, 12.63) * mm});
            skLineSegment(sketch, "E105.4", {"start": v(-37.77, 12.63) * mm, "end": v(-36.78, 10.91) * mm});
            skLineSegment(sketch, "E105.5", {"start": v(-36.78, 10.91) * mm, "end": v(-37.77, 9.2) * mm});
            skLineSegment(sketch, "E106", {"start": v(-37.79, 13.5) * mm, "end": v(-39.83, 13.5) * mm});
            skLineSegment(sketch, "E107", {"start": v(-36.08, 10.38) * mm, "end": v(-37, 8.75) * mm});
            skLineSegment(sketch, "E108.1", {"start": v(-52, 8.59) * mm, "end": v(-52.02, 8.62) * mm});
            skLineSegment(sketch, "E108.2", {"start": v(-52.02, 8.62) * mm, "end": v(-51.03, 10.34) * mm});
            skLineSegment(sketch, "E108.3", {"start": v(-51.03, 10.34) * mm, "end": v(-49.04, 10.34) * mm});
            skLineSegment(sketch, "E109", {"start": v(-51.8, 10.77) * mm, "end": v(-52.79, 9.04) * mm});
            skLineSegment(sketch, "E110.0", {"start": v(-49.05, 11.2) * mm, "end": v(-51.04, 11.2) * mm});
            skLineSegment(sketch, "E110.1", {"start": v(-51.04, 11.2) * mm, "end": v(-52.03, 12.92) * mm});
            skLineSegment(sketch, "E110.2", {"start": v(-52.03, 12.92) * mm, "end": v(-51.05, 14.62) * mm});
            skLineSegment(sketch, "E110.5", {"start": v(-48.06, 12.92) * mm, "end": v(-49.05, 11.2) * mm});
            skLineSegment(sketch, "E111", {"start": v(-52.64, 12.22) * mm, "end": v(-51.8, 10.77) * mm});
            skLineSegment(sketch, "E112.0", {"start": v(-45.33, 9.09) * mm, "end": v(-47.25, 9.09) * mm});
            skLineSegment(sketch, "E112.1", {"start": v(-47.25, 9.09) * mm, "end": v(-48.24, 10.8) * mm});
            skLineSegment(sketch, "E112.2", {"start": v(-48.24, 10.8) * mm, "end": v(-47.25, 12.52) * mm});
            skLineSegment(sketch, "E112.3", {"start": v(-47.25, 12.52) * mm, "end": v(-45.27, 12.52) * mm});
            skLineSegment(sketch, "E112.4", {"start": v(-45.27, 12.52) * mm, "end": v(-44.32, 10.83) * mm});
            skLineSegment(sketch, "E113", {"start": v(-45.34, 13.39) * mm, "end": v(-47.33, 13.39) * mm});
            skLineSegment(sketch, "E114.0", {"start": v(-26.37, 11.37) * mm, "end": v(-28.35, 11.37) * mm});
            skLineSegment(sketch, "E114.1", {"start": v(-28.35, 11.37) * mm, "end": v(-29.35, 13.09) * mm});
            skLineSegment(sketch, "E114.2", {"start": v(-29.35, 13.09) * mm, "end": v(-28.35, 14.8) * mm});
            skLineSegment(sketch, "E114.3", {"start": v(-28.35, 14.8) * mm, "end": v(-26.37, 14.8) * mm});
            skLineSegment(sketch, "E114.4", {"start": v(-26.37, 14.8) * mm, "end": v(-25.38, 13.09) * mm});
            skLineSegment(sketch, "E114.5", {"start": v(-25.38, 13.09) * mm, "end": v(-26.37, 11.37) * mm});
            skLineSegment(sketch, "E115", {"start": v(-29.15, 15.2) * mm, "end": v(-30.15, 13.44) * mm});
            skLineSegment(sketch, "E116", {"start": v(-28.3, 10.49) * mm, "end": v(-26.3, 10.49) * mm});
            skLineSegment(sketch, "E117.1", {"start": v(-28.36, 15.67) * mm, "end": v(-29.35, 17.39) * mm});
            skLineSegment(sketch, "E117.2", {"start": v(-29.35, 17.39) * mm, "end": v(-28.36, 19.1) * mm});
            skLineSegment(sketch, "E117.3", {"start": v(-28.36, 19.1) * mm, "end": v(-26.36, 19.1) * mm});
            skLineSegment(sketch, "E118", {"start": v(-29.15, 19.5) * mm, "end": v(-30.16, 17.75) * mm});
            skLineSegment(sketch, "E119.0", {"start": v(-22.58, 9.25) * mm, "end": v(-24.57, 9.25) * mm});
            skLineSegment(sketch, "E119.1", {"start": v(-24.57, 9.25) * mm, "end": v(-25.56, 10.96) * mm});
            skLineSegment(sketch, "E119.2", {"start": v(-25.56, 10.96) * mm, "end": v(-24.57, 12.68) * mm});
            skLineSegment(sketch, "E119.3", {"start": v(-24.57, 12.68) * mm, "end": v(-22.58, 12.68) * mm});
            skLineSegment(sketch, "E120", {"start": v(-26.3, 10.49) * mm, "end": v(-25.2, 8.59) * mm});
            skLineSegment(sketch, "E121.0", {"start": v(-22.6, 13.55) * mm, "end": v(-24.58, 13.55) * mm});
            skLineSegment(sketch, "E121.1", {"start": v(-24.58, 13.55) * mm, "end": v(-25.57, 15.27) * mm});
            skLineSegment(sketch, "E121.2", {"start": v(-25.57, 15.27) * mm, "end": v(-24.58, 16.99) * mm});
            skLineSegment(sketch, "E121.3", {"start": v(-24.58, 16.99) * mm, "end": v(-22.6, 16.99) * mm});
            skLineSegment(sketch, "E122.0", {"start": v(-33.87, 11.26) * mm, "end": v(-35.85, 11.26) * mm});
            skLineSegment(sketch, "E122.1", {"start": v(-35.85, 11.26) * mm, "end": v(-36.84, 12.98) * mm});
            skLineSegment(sketch, "E122.2", {"start": v(-36.84, 12.98) * mm, "end": v(-35.85, 14.7) * mm});
            skLineSegment(sketch, "E122.3", {"start": v(-35.85, 14.7) * mm, "end": v(-33.87, 14.7) * mm});
            skLineSegment(sketch, "E122.4", {"start": v(-33.87, 14.7) * mm, "end": v(-32.87, 12.98) * mm});
            skLineSegment(sketch, "E122.5", {"start": v(-32.87, 12.98) * mm, "end": v(-33.87, 11.26) * mm});
            skLineSegment(sketch, "E123", {"start": v(-36.08, 10.38) * mm, "end": v(-33.8, 10.38) * mm});
            skLineSegment(sketch, "E124.0", {"start": v(-35.84, 15.56) * mm, "end": v(-35.86, 15.56) * mm});
            skLineSegment(sketch, "E124.1", {"start": v(-35.86, 15.56) * mm, "end": v(-36.85, 17.28) * mm});
            skLineSegment(sketch, "E124.2", {"start": v(-36.85, 17.28) * mm, "end": v(-35.86, 19) * mm});
            skLineSegment(sketch, "E124.4", {"start": v(-33.86, 18.98) * mm, "end": v(-32.92, 17.34) * mm});
            skLineSegment(sketch, "E125", {"start": v(-33.14, 19.47) * mm, "end": v(-32.15, 17.75) * mm});
            skLineSegment(sketch, "E126.0", {"start": v(-30.08, 9.14) * mm, "end": v(-32.06, 9.14) * mm});
            skLineSegment(sketch, "E126.1", {"start": v(-32.06, 9.14) * mm, "end": v(-33.06, 10.86) * mm});
            skLineSegment(sketch, "E126.2", {"start": v(-33.06, 10.86) * mm, "end": v(-32.06, 12.58) * mm});
            skLineSegment(sketch, "E126.3", {"start": v(-32.06, 12.58) * mm, "end": v(-30.08, 12.58) * mm});
            skLineSegment(sketch, "E126.4", {"start": v(-30.08, 12.58) * mm, "end": v(-29.09, 10.86) * mm});
            skLineSegment(sketch, "E126.5", {"start": v(-29.09, 10.86) * mm, "end": v(-30.08, 9.14) * mm});
            skLineSegment(sketch, "E127", {"start": v(-33.8, 10.38) * mm, "end": v(-32.8, 8.67) * mm});
            skLineSegment(sketch, "E128", {"start": v(-28.3, 10.49) * mm, "end": v(-29.4, 8.67) * mm});
            skLineSegment(sketch, "E129.0", {"start": v(-30.15, 13.44) * mm, "end": v(-32.07, 13.44) * mm});
            skLineSegment(sketch, "E129.1", {"start": v(-32.07, 13.44) * mm, "end": v(-33.06, 15.16) * mm});
            skLineSegment(sketch, "E129.2", {"start": v(-33.06, 15.16) * mm, "end": v(-32.07, 16.88) * mm});
            skLineSegment(sketch, "E129.3", {"start": v(-32.07, 16.88) * mm, "end": v(-30.09, 16.88) * mm});
            skLineSegment(sketch, "E129.4", {"start": v(-30.09, 16.88) * mm, "end": v(-29.15, 15.2) * mm});
            skLineSegment(sketch, "E130", {"start": v(-30.16, 17.75) * mm, "end": v(-32.15, 17.75) * mm});
            skLineSegment(sketch, "E131.trimOffspring", {"start": v(-44.32, 15.16) * mm, "end": v(-45.34, 13.39) * mm});
            skLineSegment(sketch, "E132.trimOffspring", {"start": v(-51.81, 15.05) * mm, "end": v(-52.8, 13.35) * mm});
            skLineSegment(sketch, "E133", {"start": v(-40.55, 8.73) * mm, "end": v(-40.55, 8.67) * mm});
            skLineSegment(sketch, "E134", {"start": v(-37, 8.75) * mm, "end": v(-37, 8.67) * mm});
            skLineSegment(sketch, "E135", {"start": v(-63.22, 8.7) * mm, "end": v(-63.22, 8.67) * mm});
            skLineSegment(sketch, "E136", {"start": v(-54.88, 9.04) * mm, "end": v(-52.79, 9.04) * mm});
            skLineSegment(sketch, "E137", {"start": v(-54.87, 13.35) * mm, "end": v(-52.8, 13.35) * mm});
            skLineSegment(sketch, "E138", {"start": v(-54.98, 12.22) * mm, "end": v(-52.64, 12.22) * mm});
            skLineSegment(sketch, "E139", {"start": v(-47.33, 13.39) * mm, "end": v(-48.36, 14.99) * mm});
            skLineSegment(sketch, "E140.trimOffspring", {"start": v(-71.72, 31.87) * mm, "end": v(-71.72, 8.67) * mm});
            skLineSegment(sketch, "E141.0", {"start": v(-34.02, 28.55) * mm, "end": v(-36, 28.55) * mm});
            skLineSegment(sketch, "E141.1", {"start": v(-36, 28.55) * mm, "end": v(-37, 30.26) * mm});
            skLineSegment(sketch, "E141.2", {"start": v(-37, 30.26) * mm, "end": v(-36, 31.98) * mm});
            skLineSegment(sketch, "E141.3", {"start": v(-36, 31.98) * mm, "end": v(-34.02, 31.98) * mm});
            skLineSegment(sketch, "E141.4", {"start": v(-34.02, 31.98) * mm, "end": v(-33.03, 30.26) * mm});
            skLineSegment(sketch, "E141.5", {"start": v(-33.03, 30.26) * mm, "end": v(-34.02, 28.55) * mm});
            skLineSegment(sketch, "E142", {"start": v(-36.8, 32.37) * mm, "end": v(-37.8, 30.62) * mm});
            skLineSegment(sketch, "E143", {"start": v(-35.95, 27.67) * mm, "end": v(-33.95, 27.67) * mm});
            skLineSegment(sketch, "E144.0", {"start": v(-34.03, 32.85) * mm, "end": v(-36.01, 32.85) * mm});
            skLineSegment(sketch, "E144.1", {"start": v(-36.01, 32.85) * mm, "end": v(-37, 34.57) * mm});
            skLineSegment(sketch, "E144.2", {"start": v(-37, 34.57) * mm, "end": v(-36.17, 36.01) * mm});
            skLineSegment(sketch, "E144.4", {"start": v(-33.87, 36.01) * mm, "end": v(-33.04, 34.57) * mm});
            skLineSegment(sketch, "E144.5", {"start": v(-33.04, 34.57) * mm, "end": v(-34.03, 32.85) * mm});
            skLineSegment(sketch, "E145", {"start": v(-37.18, 36.01) * mm, "end": v(-37.81, 34.92) * mm});
            skLineSegment(sketch, "E146", {"start": v(-32.87, 36.01) * mm, "end": v(-32.3, 35.03) * mm});
            skLineSegment(sketch, "E147.0", {"start": v(-30.23, 26.42) * mm, "end": v(-32.22, 26.42) * mm});
            skLineSegment(sketch, "E147.1", {"start": v(-32.22, 26.42) * mm, "end": v(-33.21, 28.14) * mm});
            skLineSegment(sketch, "E147.2", {"start": v(-33.21, 28.14) * mm, "end": v(-32.22, 29.86) * mm});
            skLineSegment(sketch, "E147.3", {"start": v(-32.22, 29.86) * mm, "end": v(-30.24, 29.86) * mm});
            skLineSegment(sketch, "E147.4", {"start": v(-30.24, 29.86) * mm, "end": v(-30.23, 29.85) * mm});
            skLineSegment(sketch, "E147.5", {"start": v(-29.24, 28.14) * mm, "end": v(-30.23, 26.42) * mm});
            skLineSegment(sketch, "E148", {"start": v(-33.95, 27.67) * mm, "end": v(-32.93, 25.9) * mm});
            skLineSegment(sketch, "E149", {"start": v(-28.61, 27.5) * mm, "end": v(-29.44, 26.03) * mm});
            skLineSegment(sketch, "E150.0", {"start": v(-30.24, 30.73) * mm, "end": v(-32.23, 30.73) * mm});
            skLineSegment(sketch, "E150.1", {"start": v(-32.23, 30.73) * mm, "end": v(-33.22, 32.45) * mm});
            skLineSegment(sketch, "E150.2", {"start": v(-33.22, 32.45) * mm, "end": v(-32.23, 34.17) * mm});
            skLineSegment(sketch, "E150.3", {"start": v(-32.23, 34.17) * mm, "end": v(-30.24, 34.17) * mm});
            skLineSegment(sketch, "E150.4", {"start": v(-30.24, 34.17) * mm, "end": v(-29.25, 32.45) * mm});
            skLineSegment(sketch, "E150.5", {"start": v(-29.25, 32.45) * mm, "end": v(-30.24, 30.73) * mm});
            skLineSegment(sketch, "E151", {"start": v(-30.03, 35.03) * mm, "end": v(-32.3, 35.03) * mm});
            skLineSegment(sketch, "E152", {"start": v(-32.23, 29.85) * mm, "end": v(-30.23, 29.85) * mm});
            skLineSegment(sketch, "E153.0", {"start": v(-41.52, 28.44) * mm, "end": v(-43.5, 28.44) * mm});
            skLineSegment(sketch, "E153.1", {"start": v(-43.5, 28.44) * mm, "end": v(-44.5, 30.16) * mm});
            skLineSegment(sketch, "E153.2", {"start": v(-44.5, 30.16) * mm, "end": v(-43.5, 31.88) * mm});
            skLineSegment(sketch, "E153.3", {"start": v(-43.5, 31.88) * mm, "end": v(-41.52, 31.88) * mm});
            skLineSegment(sketch, "E153.4", {"start": v(-41.52, 31.88) * mm, "end": v(-40.53, 30.16) * mm});
            skLineSegment(sketch, "E153.5", {"start": v(-40.53, 30.16) * mm, "end": v(-41.52, 28.44) * mm});
            skLineSegment(sketch, "E154", {"start": v(-43.77, 27.56) * mm, "end": v(-41.44, 27.56) * mm});
            skLineSegment(sketch, "E155.0", {"start": v(-41.53, 32.74) * mm, "end": v(-43.51, 32.74) * mm});
            skLineSegment(sketch, "E155.1", {"start": v(-43.51, 32.74) * mm, "end": v(-44.5, 34.46) * mm});
            skLineSegment(sketch, "E155.2", {"start": v(-44.5, 34.46) * mm, "end": v(-43.6, 36.03) * mm});
            skLineSegment(sketch, "E155.4", {"start": v(-41.44, 36.03) * mm, "end": v(-40.53, 34.46) * mm});
            skLineSegment(sketch, "E155.5", {"start": v(-40.53, 34.46) * mm, "end": v(-41.53, 32.74) * mm});
            skLineSegment(sketch, "E156", {"start": v(-44.61, 36.02) * mm, "end": v(-45.22, 34.97) * mm});
            skLineSegment(sketch, "E157", {"start": v(-40.44, 36.03) * mm, "end": v(-39.8, 34.92) * mm});
            skLineSegment(sketch, "E158.0", {"start": v(-37.73, 26.32) * mm, "end": v(-39.72, 26.32) * mm});
            skLineSegment(sketch, "E158.1", {"start": v(-39.72, 26.32) * mm, "end": v(-40.7, 28.04) * mm});
            skLineSegment(sketch, "E158.2", {"start": v(-40.7, 28.04) * mm, "end": v(-39.72, 29.76) * mm});
            skLineSegment(sketch, "E158.3", {"start": v(-39.72, 29.76) * mm, "end": v(-37.73, 29.76) * mm});
            skLineSegment(sketch, "E158.4", {"start": v(-37.73, 29.76) * mm, "end": v(-36.74, 28.04) * mm});
            skLineSegment(sketch, "E158.5", {"start": v(-36.74, 28.04) * mm, "end": v(-37.73, 26.32) * mm});
            skLineSegment(sketch, "E159", {"start": v(-41.44, 27.56) * mm, "end": v(-40.43, 25.8) * mm});
            skLineSegment(sketch, "E160", {"start": v(-35.95, 27.67) * mm, "end": v(-36.94, 25.93) * mm});
            skLineSegment(sketch, "E161.0", {"start": v(-37.8, 30.62) * mm, "end": v(-39.72, 30.62) * mm});
            skLineSegment(sketch, "E161.1", {"start": v(-39.72, 30.62) * mm, "end": v(-40.72, 32.34) * mm});
            skLineSegment(sketch, "E161.2", {"start": v(-40.72, 32.34) * mm, "end": v(-39.72, 34.06) * mm});
            skLineSegment(sketch, "E161.3", {"start": v(-39.72, 34.06) * mm, "end": v(-37.74, 34.06) * mm});
            skLineSegment(sketch, "E161.4", {"start": v(-37.74, 34.06) * mm, "end": v(-36.8, 32.37) * mm});
            skLineSegment(sketch, "E162", {"start": v(-37.81, 34.92) * mm, "end": v(-39.8, 34.92) * mm});
            skLineSegment(sketch, "E163.2", {"start": v(-33.12, 19.5) * mm, "end": v(-32.13, 21.22) * mm});
            skLineSegment(sketch, "E163.3", {"start": v(-32.13, 21.22) * mm, "end": v(-30.14, 21.22) * mm});
            skLineSegment(sketch, "E163.4", {"start": v(-30.14, 21.22) * mm, "end": v(-29.15, 19.5) * mm});
            skLineSegment(sketch, "E164", {"start": v(-32.92, 21.6) * mm, "end": v(-33.93, 19.86) * mm});
            skLineSegment(sketch, "E165.0", {"start": v(-30.15, 22.09) * mm, "end": v(-32.14, 22.09) * mm});
            skLineSegment(sketch, "E165.1", {"start": v(-32.14, 22.09) * mm, "end": v(-33.13, 23.8) * mm});
            skLineSegment(sketch, "E165.2", {"start": v(-33.13, 23.8) * mm, "end": v(-32.14, 25.53) * mm});
            skLineSegment(sketch, "E165.3", {"start": v(-32.14, 25.53) * mm, "end": v(-30.15, 25.53) * mm});
            skLineSegment(sketch, "E165.4", {"start": v(-30.15, 25.53) * mm, "end": v(-29.16, 23.8) * mm});
            skLineSegment(sketch, "E165.5", {"start": v(-29.16, 23.8) * mm, "end": v(-30.15, 22.09) * mm});
            skLineSegment(sketch, "E166", {"start": v(-32.93, 25.9) * mm, "end": v(-33.94, 24.17) * mm});
            skLineSegment(sketch, "E167", {"start": v(-29.44, 26.03) * mm, "end": v(-28.43, 24.27) * mm});
            skLineSegment(sketch, "E168.4", {"start": v(-26.36, 19.1) * mm, "end": v(-25.36, 17.38) * mm});
            skLineSegment(sketch, "E168.5", {"start": v(-25.36, 17.38) * mm, "end": v(-26.35, 15.67) * mm});
            skLineSegment(sketch, "E169.0", {"start": v(-26.37, 19.97) * mm, "end": v(-28.35, 19.97) * mm});
            skLineSegment(sketch, "E169.1", {"start": v(-28.35, 19.97) * mm, "end": v(-29.34, 21.69) * mm});
            skLineSegment(sketch, "E169.2", {"start": v(-29.34, 21.69) * mm, "end": v(-28.35, 23.4) * mm});
            skLineSegment(sketch, "E169.3", {"start": v(-28.35, 23.4) * mm, "end": v(-26.37, 23.4) * mm});
            skLineSegment(sketch, "E169.4", {"start": v(-26.37, 23.4) * mm, "end": v(-25.37, 21.69) * mm});
            skLineSegment(sketch, "E169.5", {"start": v(-25.37, 21.69) * mm, "end": v(-26.37, 19.97) * mm});
            skLineSegment(sketch, "E170", {"start": v(-26.16, 24.27) * mm, "end": v(-28.43, 24.27) * mm});
            skLineSegment(sketch, "E171.0", {"start": v(-37.64, 17.68) * mm, "end": v(-39.62, 17.68) * mm});
            skLineSegment(sketch, "E171.1", {"start": v(-39.62, 17.68) * mm, "end": v(-40.62, 19.4) * mm});
            skLineSegment(sketch, "E171.2", {"start": v(-40.62, 19.4) * mm, "end": v(-39.62, 21.12) * mm});
            skLineSegment(sketch, "E171.3", {"start": v(-39.62, 21.12) * mm, "end": v(-37.64, 21.12) * mm});
            skLineSegment(sketch, "E171.4", {"start": v(-37.64, 21.12) * mm, "end": v(-36.65, 19.4) * mm});
            skLineSegment(sketch, "E171.5", {"start": v(-36.65, 19.4) * mm, "end": v(-37.64, 17.68) * mm});
            skLineSegment(sketch, "E172", {"start": v(-39.89, 16.8) * mm, "end": v(-37.57, 16.8) * mm});
            skLineSegment(sketch, "E173.0", {"start": v(-37.65, 21.98) * mm, "end": v(-39.63, 21.98) * mm});
            skLineSegment(sketch, "E173.1", {"start": v(-39.63, 21.98) * mm, "end": v(-40.62, 23.7) * mm});
            skLineSegment(sketch, "E173.2", {"start": v(-40.62, 23.7) * mm, "end": v(-39.63, 25.42) * mm});
            skLineSegment(sketch, "E173.3", {"start": v(-39.63, 25.42) * mm, "end": v(-37.65, 25.42) * mm});
            skLineSegment(sketch, "E173.4", {"start": v(-37.65, 25.42) * mm, "end": v(-36.66, 23.7) * mm});
            skLineSegment(sketch, "E173.5", {"start": v(-36.66, 23.7) * mm, "end": v(-37.65, 21.98) * mm});
            skLineSegment(sketch, "E174", {"start": v(-40.43, 25.8) * mm, "end": v(-41.34, 24.22) * mm});
            skLineSegment(sketch, "E175", {"start": v(-39.63, 21.1) * mm, "end": v(-37.63, 21.1) * mm});
            skLineSegment(sketch, "E176", {"start": v(-36.94, 25.93) * mm, "end": v(-35.92, 24.17) * mm});
            skLineSegment(sketch, "E177.0", {"start": v(-33.85, 15.56) * mm, "end": v(-35.84, 15.56) * mm});
            skLineSegment(sketch, "E177.1", {"start": v(-35.84, 15.56) * mm, "end": v(-35.84, 15.56) * mm});
            skLineSegment(sketch, "E177.4", {"start": v(-33.85, 19) * mm, "end": v(-32.86, 17.28) * mm});
            skLineSegment(sketch, "E177.5", {"start": v(-32.86, 17.28) * mm, "end": v(-33.85, 15.56) * mm});
            skLineSegment(sketch, "E178", {"start": v(-37.57, 16.8) * mm, "end": v(-36.71, 15.32) * mm});
            skLineSegment(sketch, "E179.0", {"start": v(-33.93, 19.86) * mm, "end": v(-35.85, 19.86) * mm});
            skLineSegment(sketch, "E179.1", {"start": v(-35.85, 19.86) * mm, "end": v(-36.84, 21.58) * mm});
            skLineSegment(sketch, "E179.2", {"start": v(-36.84, 21.58) * mm, "end": v(-35.85, 23.3) * mm});
            skLineSegment(sketch, "E179.3", {"start": v(-35.85, 23.3) * mm, "end": v(-33.86, 23.3) * mm});
            skLineSegment(sketch, "E179.4", {"start": v(-33.86, 23.3) * mm, "end": v(-32.92, 21.6) * mm});
            skLineSegment(sketch, "E180", {"start": v(-33.94, 24.17) * mm, "end": v(-35.92, 24.17) * mm});
            skLineSegment(sketch, "E181", {"start": v(-33.86, 18.98) * mm, "end": v(-33.85, 18.98) * mm});
            skLineSegment(sketch, "E182.0", {"start": v(-26.4, 28.38) * mm, "end": v(-28.38, 28.38) * mm});
            skLineSegment(sketch, "E182.1", {"start": v(-28.38, 28.38) * mm, "end": v(-29.38, 30.1) * mm});
            skLineSegment(sketch, "E182.2", {"start": v(-29.38, 30.1) * mm, "end": v(-28.39, 31.81) * mm});
            skLineSegment(sketch, "E182.3", {"start": v(-28.39, 31.81) * mm, "end": v(-26.4, 31.81) * mm});
            skLineSegment(sketch, "E182.4", {"start": v(-26.4, 31.81) * mm, "end": v(-25.4, 30.1) * mm});
            skLineSegment(sketch, "E182.5", {"start": v(-25.4, 30.1) * mm, "end": v(-26.4, 28.38) * mm});
            skLineSegment(sketch, "E183", {"start": v(-30.26, 29.86) * mm, "end": v(-29.25, 28.13) * mm});
            skLineSegment(sketch, "E184", {"start": v(-28.61, 27.5) * mm, "end": v(-26.33, 27.5) * mm});
            skLineSegment(sketch, "E185.0", {"start": v(-26.4, 32.68) * mm, "end": v(-28.4, 32.68) * mm});
            skLineSegment(sketch, "E185.1", {"start": v(-28.4, 32.68) * mm, "end": v(-29.39, 34.4) * mm});
            skLineSegment(sketch, "E185.2", {"start": v(-29.39, 34.4) * mm, "end": v(-28.45, 36.01) * mm});
            skLineSegment(sketch, "E185.4", {"start": v(-26.35, 36.01) * mm, "end": v(-25.42, 34.4) * mm});
            skLineSegment(sketch, "E185.5", {"start": v(-25.42, 34.4) * mm, "end": v(-26.4, 32.68) * mm});
            skLineSegment(sketch, "E186", {"start": v(-29.47, 36.01) * mm, "end": v(-30.03, 35.03) * mm});
            skLineSegment(sketch, "E187", {"start": v(-25.35, 36.01) * mm, "end": v(-24.68, 34.86) * mm});
            skLineSegment(sketch, "E188.0", {"start": v(-22.61, 26.26) * mm, "end": v(-24.6, 26.26) * mm});
            skLineSegment(sketch, "E188.1", {"start": v(-24.6, 26.26) * mm, "end": v(-25.6, 27.97) * mm});
            skLineSegment(sketch, "E188.2", {"start": v(-25.6, 27.97) * mm, "end": v(-24.6, 29.7) * mm});
            skLineSegment(sketch, "E188.3", {"start": v(-24.6, 29.7) * mm, "end": v(-22.61, 29.7) * mm});
            skLineSegment(sketch, "E189", {"start": v(-26.33, 27.5) * mm, "end": v(-25.31, 25.74) * mm});
            skLineSegment(sketch, "E190.0", {"start": v(-22.69, 30.56) * mm, "end": v(-24.6, 30.56) * mm});
            skLineSegment(sketch, "E190.1", {"start": v(-24.6, 30.56) * mm, "end": v(-25.6, 32.28) * mm});
            skLineSegment(sketch, "E190.2", {"start": v(-25.6, 32.28) * mm, "end": v(-24.6, 34) * mm});
            skLineSegment(sketch, "E190.3", {"start": v(-24.6, 34) * mm, "end": v(-22.62, 34) * mm});
            skLineSegment(sketch, "E191", {"start": v(-22.76, 34.86) * mm, "end": v(-24.68, 34.86) * mm});
            skLineSegment(sketch, "E192", {"start": v(-25.31, 25.74) * mm, "end": v(-26.16, 24.27) * mm});
            skLineSegment(sketch, "E193", {"start": v(-40.88, 15.05) * mm, "end": v(-39.83, 13.5) * mm});
            skLineSegment(sketch, "E194", {"start": v(-37.79, 13.5) * mm, "end": v(-36.71, 15.32) * mm});
            skLineSegment(sketch, "E195", {"start": v(-33.85, 19) * mm, "end": v(-35.86, 19) * mm});
            skLineSegment(sketch, "E196", {"start": v(-26.36, 19.1) * mm, "end": v(-26.36, 19.1) * mm});
            skLineSegment(sketch, "E197", {"start": v(-33.12, 19.5) * mm, "end": v(-33.14, 19.47) * mm});
            skLineSegment(sketch, "E198", {"start": v(-71.72, 32.73) * mm, "end": v(-71.72, 31.87) * mm});
            skLineSegment(sketch, "E199.trimOffspring", {"start": v(-19.72, 0.67) * mm, "end": v(-13.72, 0.67) * mm});
            skLineSegment(sketch, "E200", {"start": v(-77.72, 39.57) * mm, "end": v(-13.72, 39.57) * mm});
            skLineSegment(sketch, "E201.bottom", {"start": v(-13.72, 6.87) * mm, "end": v(-9.56, 6.87) * mm});
            skLineSegment(sketch, "E201.top", {"start": v(-13.72, 33.3) * mm, "end": v(-9.56, 33.3) * mm});
            skLineSegment(sketch, "E201.left", {"start": v(-13.72, 6.87) * mm, "end": v(-13.72, 33.3) * mm});
            skLineSegment(sketch, "E201.right", {"start": v(-5.72, 10.7) * mm, "end": v(-5.72, 29.47) * mm});
            skArc(sketch, "E202.filletArc", {"start": v(-5.72, 29.47) * mm, "mid": v(-6.85, 32.18) * mm, "end": v(-9.56, 33.3) * mm});
            skPoint(sketch, "E203.visualSharp", {"position": v(-5.72, 6.87) * mm});
            skArc(sketch, "E203.filletArc", {"start": v(-9.56, 6.87) * mm, "mid": v(-6.85, 8) * mm, "end": v(-5.72, 10.7) * mm});
            skLineSegment(sketch, "E204.right", {"start": v(-13.72, 39.57) * mm, "end": v(-13.72, 33.3) * mm});
            skLineSegment(sketch, "E205.right", {"start": v(-13.72, 11.56) * mm, "end": v(-13.72, 8.67) * mm});
            skLineSegment(sketch, "E206", {"start": v(-6.02, 9.22) * mm, "end": v(-6.02, 30.95) * mm});
            skLineSegment(sketch, "E207", {"start": v(-71.72, 0.67) * mm, "end": v(-19.72, 0.67) * mm});
            skLineSegment(sketch, "E208", {"start": v(-71.72, 8.67) * mm, "end": v(-19.72, 8.67) * mm});
            skLineSegment(sketch, "E209", {"start": v(-19.72, 36.1) * mm, "end": v(-71.72, 36.1) * mm});
            skLineSegment(sketch, "E210", {"start": v(-49.04, 10.34) * mm, "end": v(-48.08, 8.67) * mm});
            skLineSegment(sketch, "E211", {"start": v(-66.07, 10.2) * mm, "end": v(-67.02, 8.67) * mm});
            skLineSegment(sketch, "E212", {"start": v(-59.24, 9.15) * mm, "end": v(-59.53, 8.67) * mm});
            skLineSegment(sketch, "E213", {"start": v(-49.04, 14.62) * mm, "end": v(-48.06, 12.92) * mm});
            skLineSegment(sketch, "E214", {"start": v(-70.16, 34.83) * mm, "end": v(-70.87, 36.1) * mm});
            skLineSegment(sketch, "E215", {"start": v(-32.87, 36.01) * mm, "end": v(-32.92, 36.1) * mm});
            skLineSegment(sketch, "E216", {"start": v(-29.47, 36.01) * mm, "end": v(-29.47, 36.1) * mm});
            skLineSegment(sketch, "E217", {"start": v(-25.35, 36.01) * mm, "end": v(-25.35, 36.01) * mm});
            skLineSegment(sketch, "E218.trimOffspring", {"start": v(-26.35, 15.67) * mm, "end": v(-28.36, 15.67) * mm});
            skLineSegment(sketch, "E219", {"start": v(-63.4, 34.47) * mm, "end": v(-64.34, 36.1) * mm});
            skLineSegment(sketch, "E220", {"start": v(-62.66, 34.94) * mm, "end": v(-63.3, 36.1) * mm});
            skLineSegment(sketch, "E221", {"start": v(-58.8, 36.01) * mm, "end": v(-56.69, 36.01) * mm});
            skLineSegment(sketch, "E222", {"start": v(-55.69, 36.01) * mm, "end": v(-55.69, 36.1) * mm});
            skLineSegment(sketch, "E223", {"start": v(-52.38, 36.01) * mm, "end": v(-52.38, 36.1) * mm});
            skLineSegment(sketch, "E224", {"start": v(-59.81, 36.01) * mm, "end": v(-59.81, 36.1) * mm});
            skLineSegment(sketch, "E225", {"start": v(-51.36, 36.01) * mm, "end": v(-49.13, 36.01) * mm});
            skLineSegment(sketch, "E226", {"start": v(-48.13, 36.01) * mm, "end": v(-48.23, 36.1) * mm});
            skLineSegment(sketch, "E227", {"start": v(-44.61, 36.02) * mm, "end": v(-44.52, 36.1) * mm});
            skLineSegment(sketch, "E228", {"start": v(-37.18, 36.01) * mm, "end": v(-37.07, 36.1) * mm});
            skLineSegment(sketch, "E229", {"start": v(-40.44, 36.03) * mm, "end": v(-40.44, 36.1) * mm});
            skLineSegment(sketch, "E230", {"start": v(-21.64, 11) * mm, "end": v(-22.65, 9.25) * mm});
            skLineSegment(sketch, "E231.0", {"start": v(-22.65, 9.25) * mm, "end": v(-24.57, 9.25) * mm});
            skLineSegment(sketch, "E231.4", {"start": v(-22.58, 12.68) * mm, "end": v(-21.64, 11) * mm});
            skLineSegment(sketch, "E232", {"start": v(-21.65, 15.3) * mm, "end": v(-22.65, 13.55) * mm});
            skLineSegment(sketch, "E233.0", {"start": v(-22.65, 13.55) * mm, "end": v(-24.57, 13.55) * mm});
            skLineSegment(sketch, "E233.1", {"start": v(-24.57, 13.55) * mm, "end": v(-25.57, 15.27) * mm});
            skLineSegment(sketch, "E233.2", {"start": v(-25.57, 15.27) * mm, "end": v(-24.57, 16.98) * mm});
            skLineSegment(sketch, "E233.3", {"start": v(-24.57, 16.98) * mm, "end": v(-22.6, 16.98) * mm});
            skLineSegment(sketch, "E233.4", {"start": v(-22.6, 16.98) * mm, "end": v(-21.65, 15.3) * mm});
            skLineSegment(sketch, "E234", {"start": v(-21.7, 19.6) * mm, "end": v(-22.7, 17.85) * mm});
            skLineSegment(sketch, "E235.0", {"start": v(-22.7, 17.85) * mm, "end": v(-24.63, 17.85) * mm});
            skLineSegment(sketch, "E235.1", {"start": v(-24.63, 17.85) * mm, "end": v(-25.62, 19.57) * mm});
            skLineSegment(sketch, "E235.2", {"start": v(-25.62, 19.57) * mm, "end": v(-24.63, 21.3) * mm});
            skLineSegment(sketch, "E235.3", {"start": v(-24.63, 21.3) * mm, "end": v(-22.65, 21.3) * mm});
            skLineSegment(sketch, "E235.4", {"start": v(-22.65, 21.3) * mm, "end": v(-21.7, 19.6) * mm});
            skLineSegment(sketch, "E236", {"start": v(-21.64, 23.8) * mm, "end": v(-22.65, 22.06) * mm});
            skLineSegment(sketch, "E237.0", {"start": v(-22.65, 22.06) * mm, "end": v(-24.57, 22.06) * mm});
            skLineSegment(sketch, "E237.1", {"start": v(-24.57, 22.06) * mm, "end": v(-25.56, 23.78) * mm});
            skLineSegment(sketch, "E237.2", {"start": v(-25.56, 23.78) * mm, "end": v(-24.57, 25.5) * mm});
            skLineSegment(sketch, "E237.3", {"start": v(-24.57, 25.5) * mm, "end": v(-22.59, 25.5) * mm});
            skLineSegment(sketch, "E237.4", {"start": v(-22.59, 25.5) * mm, "end": v(-21.64, 23.8) * mm});
            skLineSegment(sketch, "E238", {"start": v(-21.67, 28) * mm, "end": v(-22.68, 26.26) * mm});
            skLineSegment(sketch, "E239.0", {"start": v(-22.68, 26.26) * mm, "end": v(-24.6, 26.26) * mm});
            skLineSegment(sketch, "E239.4", {"start": v(-22.61, 29.7) * mm, "end": v(-21.67, 28) * mm});
            skLineSegment(sketch, "E240", {"start": v(-21.68, 32.3) * mm, "end": v(-22.69, 30.56) * mm});
            skLineSegment(sketch, "E241.4", {"start": v(-22.62, 34) * mm, "end": v(-21.68, 32.3) * mm});
            skLineSegment(sketch, "E242", {"start": v(-22.05, 36.1) * mm, "end": v(-22.76, 34.86) * mm});
            skLineSegment(sketch, "E243.1", {"start": v(-24.68, 34.86) * mm, "end": v(-25.4, 36.1) * mm});
            skLineSegment(sketch, "E244.0", {"start": v(-19.72, 32.66) * mm, "end": v(-21.04, 32.66) * mm});
            skLineSegment(sketch, "E244.1", {"start": v(-21.04, 32.66) * mm, "end": v(-22.03, 34.38) * mm});
            skLineSegment(sketch, "E244.2", {"start": v(-22.03, 34.38) * mm, "end": v(-21.04, 36.1) * mm});
            skLineSegment(sketch, "E244.3", {"start": v(-21.04, 36.1) * mm, "end": v(-19.72, 36.1) * mm});
            skLineSegment(sketch, "E245.0", {"start": v(-19.72, 28.36) * mm, "end": v(-20.97, 28.36) * mm});
            skLineSegment(sketch, "E245.1", {"start": v(-20.97, 28.36) * mm, "end": v(-21.96, 30.08) * mm});
            skLineSegment(sketch, "E245.2", {"start": v(-21.96, 30.08) * mm, "end": v(-20.97, 31.8) * mm});
            skLineSegment(sketch, "E245.3", {"start": v(-20.97, 31.8) * mm, "end": v(-19.72, 31.8) * mm});
            skLineSegment(sketch, "E246.0", {"start": v(-19.72, 24.11) * mm, "end": v(-20.9, 24.11) * mm});
            skLineSegment(sketch, "E246.1", {"start": v(-20.9, 24.11) * mm, "end": v(-21.89, 25.83) * mm});
            skLineSegment(sketch, "E246.2", {"start": v(-21.89, 25.83) * mm, "end": v(-20.9, 27.55) * mm});
            skLineSegment(sketch, "E246.3", {"start": v(-20.9, 27.55) * mm, "end": v(-19.72, 27.55) * mm});
            skLineSegment(sketch, "E247.0", {"start": v(-19.72, 19.88) * mm, "end": v(-20.88, 19.88) * mm});
            skLineSegment(sketch, "E247.1", {"start": v(-20.88, 19.88) * mm, "end": v(-21.87, 21.6) * mm});
            skLineSegment(sketch, "E247.2", {"start": v(-21.87, 21.6) * mm, "end": v(-20.88, 23.31) * mm});
            skLineSegment(sketch, "E247.3", {"start": v(-20.88, 23.31) * mm, "end": v(-19.72, 23.31) * mm});
            skLineSegment(sketch, "E248.0", {"start": v(-19.72, 15.65) * mm, "end": v(-20.83, 15.65) * mm});
            skLineSegment(sketch, "E248.1", {"start": v(-20.83, 15.65) * mm, "end": v(-21.82, 17.37) * mm});
            skLineSegment(sketch, "E248.2", {"start": v(-21.82, 17.37) * mm, "end": v(-20.83, 19.09) * mm});
            skLineSegment(sketch, "E248.3", {"start": v(-20.83, 19.09) * mm, "end": v(-19.72, 19.09) * mm});
            skLineSegment(sketch, "E249.0", {"start": v(-19.72, 11.42) * mm, "end": v(-20.88, 11.42) * mm});
            skLineSegment(sketch, "E249.1", {"start": v(-20.88, 11.42) * mm, "end": v(-21.87, 13.14) * mm});
            skLineSegment(sketch, "E249.2", {"start": v(-21.87, 13.14) * mm, "end": v(-20.88, 14.86) * mm});
            skLineSegment(sketch, "E249.3", {"start": v(-20.88, 14.86) * mm, "end": v(-19.72, 14.86) * mm});
            skLineSegment(sketch, "E250.1", {"start": v(-21.87, 8.67) * mm, "end": v(-21.94, 8.8) * mm});
            skLineSegment(sketch, "E250.2", {"start": v(-21.94, 8.8) * mm, "end": v(-20.95, 10.51) * mm});
            skLineSegment(sketch, "E250.3", {"start": v(-20.95, 10.51) * mm, "end": v(-19.72, 10.51) * mm});
            skLineSegment(sketch, "E251", {"start": v(-70.7, 34.3) * mm, "end": v(-71.71, 32.56) * mm});
            skLineSegment(sketch, "E252.0", {"start": v(-71.71, 32.56) * mm, "end": v(-71.72, 32.56) * mm});
            skLineSegment(sketch, "E252.3", {"start": v(-71.72, 36) * mm, "end": v(-71.65, 36) * mm});
            skLineSegment(sketch, "E252.4", {"start": v(-71.65, 36) * mm, "end": v(-70.7, 34.3) * mm});
            skLineSegment(sketch, "E253", {"start": v(-70.77, 30.16) * mm, "end": v(-71.78, 28.41) * mm});
            skLineSegment(sketch, "E254.3", {"start": v(-71.72, 31.85) * mm, "end": v(-71.72, 31.85) * mm});
            skLineSegment(sketch, "E254.4", {"start": v(-71.72, 31.85) * mm, "end": v(-70.77, 30.16) * mm});
            skLineSegment(sketch, "E255", {"start": v(-70.77, 25.85) * mm, "end": v(-71.78, 24.1) * mm});
            skLineSegment(sketch, "E256.3", {"start": v(-71.72, 27.54) * mm, "end": v(-71.71, 27.54) * mm});
            skLineSegment(sketch, "E256.4", {"start": v(-71.71, 27.54) * mm, "end": v(-70.77, 25.85) * mm});
            skLineSegment(sketch, "E257", {"start": v(-70.67, 21.58) * mm, "end": v(-71.68, 19.83) * mm});
            skLineSegment(sketch, "E258.0", {"start": v(-71.68, 19.83) * mm, "end": v(-71.72, 19.83) * mm});
            skLineSegment(sketch, "E258.3", {"start": v(-71.72, 23.27) * mm, "end": v(-71.61, 23.27) * mm});
            skLineSegment(sketch, "E258.4", {"start": v(-71.61, 23.27) * mm, "end": v(-70.67, 21.58) * mm});
            skLineSegment(sketch, "E259", {"start": v(-70.62, 17.25) * mm, "end": v(-71.63, 15.5) * mm});
            skLineSegment(sketch, "E260.0", {"start": v(-71.63, 15.5) * mm, "end": v(-71.72, 15.5) * mm});
            skLineSegment(sketch, "E260.3", {"start": v(-71.72, 18.94) * mm, "end": v(-71.57, 18.94) * mm});
            skLineSegment(sketch, "E260.4", {"start": v(-71.57, 18.94) * mm, "end": v(-70.62, 17.25) * mm});
            skLineSegment(sketch, "E261", {"start": v(-70.72, 12.83) * mm, "end": v(-71.73, 11.08) * mm});
            skLineSegment(sketch, "E262.3", {"start": v(-71.72, 14.52) * mm, "end": v(-71.66, 14.52) * mm});
            skLineSegment(sketch, "E262.4", {"start": v(-71.66, 14.52) * mm, "end": v(-70.72, 12.83) * mm});
            skLineSegment(sketch, "E263.3", {"start": v(-71.72, 10.26) * mm, "end": v(-71.6, 10.26) * mm});
            skLineSegment(sketch, "E263.4", {"start": v(-71.6, 10.26) * mm, "end": v(-70.71, 8.67) * mm});
            skSolve(sketch);
        }
        {
            var Q0;
            {var subQ4=sQuery(id+"F0.wireOp",EDGE,"E1.right");Q0=makeQuery(id+"F0.imprint","IMPRINT",FACE,{"disambiguationData":[TD([[makeQuery(id+"F0.imprint","IMPRINT",EDGE,{"derivedFrom":subQ4}),-1.0]])]});}
            var Q1;
            {var subQ1=sQuery(id+"F0.wireOp",EDGE,"hi0ildKH-8xMm-FrZD-iou3-4SPbyZ6CL9zf.right");Q1=makeQuery(id+"F0.imprint","IMPRINT",FACE,{"disambiguationData":[TD([[makeQuery(id+"F0.imprint","IMPRINT",EDGE,{"derivedFrom":subQ1}),1.0]])]});}
            var Q2;
            {var subQ1=sQuery(id+"F0.wireOp",EDGE,"hi0ildKH-8xMm-FrZD-iou3-4SPbyZ6CL9zf.bottom");Q2=makeQuery(id+"F0.imprint","IMPRINT",FACE,{"disambiguationData":[TD([[makeQuery(id+"F0.imprint","IMPRINT",EDGE,{"derivedFrom":subQ1}),1.0]])]});}
            var Q3;
            Q3=makeQuery(id+"F0.imprint","IMPRINT",FACE,{"disambiguationData":[TD([[makeQuery(id+"F0.imprint","IMPRINT",EDGE,{"derivedFrom":sQuery(id+"F0.wireOp",EDGE,"E6.right")}),-1.0]])]});
            var Q4;
            {var subQ1=sQuery(id+"F0.wireOp",EDGE,"E2.top");Q4=makeQuery(id+"F0.imprint","IMPRINT",FACE,{"disambiguationData":[TD([[makeQuery(id+"F0.imprint","IMPRINT",EDGE,{"derivedFrom":subQ1}),-1.0]])]});}
            var Q5;
            {var subQ0=sQuery(id+"F0.wireOp",EDGE,"E201.right");Q5=makeQuery(id+"F0.imprint","IMPRINT",FACE,{"disambiguationData":[TD([[makeQuery(id+"F0.imprint","IMPRINT",EDGE,{"derivedFrom":subQ0}),1.0]])]});}
            var Q6;
            {var subQ4=sQuery(id+"F0.wireOp",EDGE,"E201.bottom");Q6=makeQuery(id+"F0.imprint","IMPRINT",FACE,{"disambiguationData":[TD([[makeQuery(id+"F0.imprint","IMPRINT",EDGE,{"derivedFrom":subQ4}),1.0]])]});}
            extrude(context, id + "F1", {"entities" : qUnion([Q0, Q1, Q2, Q3, Q4, Q5, Q6]), "depth" : 6 * mm});
        }
        {
            var Q0;
            {var subQ1=sQuery(id+"F0.wireOp",EDGE,"E2.top");Q0=makeQuery(id+"F0.imprint","IMPRINT",FACE,{"disambiguationData":[TD([[makeQuery(id+"F0.imprint","IMPRINT",EDGE,{"derivedFrom":subQ1}),-1.0]])]});}
            var Q1;
            {var subQ4=sQuery(id+"F0.wireOp",EDGE,"E201.bottom");Q1=makeQuery(id+"F0.imprint","IMPRINT",FACE,{"disambiguationData":[TD([[makeQuery(id+"F0.imprint","IMPRINT",EDGE,{"derivedFrom":subQ4}),1.0]])]});}
            extrude(context, id + "F2", {"entities" : qUnion([Q0, Q1]), "operationType" : NewBodyOperationType.REMOVE, "depth" : 2 * mm});
        }
        {
            var Q0;
            Q0=makeQuery(id+"F0.imprint","IMPRINT",FACE,{"disambiguationData":[TD([[makeQuery(id+"F0.imprint","IMPRINT",EDGE,{"derivedFrom":sQuery(id+"F0.wireOp",EDGE,"E6.right")}),-1.0]])]});
            extrude(context, id + "F3", {"entities" : qUnion([Q0]), "operationType" : NewBodyOperationType.ADD, "depth" : 8 * mm});
        }
        {
            var Q0;
            Q0=qCreatedBy(makeId("Top.planeOp"),FACE);
            var sketch = newSketch(context, id + "F4", { "sketchPlane" : qUnion([Q0])});
            skLineSegment(sketch, "E264.bottom", {"start": v(67.63, -6) * mm, "end": v(12.13, -6) * mm});
            skLineSegment(sketch, "E264.top", {"start": v(67.63, -2) * mm, "end": v(12.13, -2) * mm});
            skLineSegment(sketch, "E264.left", {"start": v(67.63, -6) * mm, "end": v(67.63, -2) * mm});
            skLineSegment(sketch, "E264.right", {"start": v(-75.37, -6) * mm, "end": v(-75.37, -2) * mm});
            skLineSegment(sketch, "E265", {"start": v(45.13, -6) * mm, "end": v(45.13, -2) * mm});
            skLineSegment(sketch, "E266", {"start": v(-52.87, -6) * mm, "end": v(-52.87, -2) * mm});
            skLineSegment(sketch, "E267", {"start": v(-52.87, -2) * mm, "end": v(-52.87, -4) * mm});
            skLineSegment(sketch, "E268", {"start": v(-42.87, -6) * mm, "end": v(-42.87, -2) * mm});
            skLineSegment(sketch, "E269", {"start": v(35.13, -6) * mm, "end": v(35.13, -2) * mm});
            skLineSegment(sketch, "E270", {"start": v(12.13, -6) * mm, "end": v(12.13, -2) * mm});
            skLineSegment(sketch, "E271", {"start": v(-19.87, -6) * mm, "end": v(-19.87, -2) * mm});
            skLineSegment(sketch, "E272", {"start": v(-19.87, -2) * mm, "end": v(-19.87, -4) * mm});
            skLineSegment(sketch, "E273.trimOffspring", {"start": v(-19.87, -6) * mm, "end": v(-75.37, -6) * mm});
            skLineSegment(sketch, "E274.trimOffspring", {"start": v(-19.87, -2) * mm, "end": v(-75.37, -2) * mm});
            skSolve(sketch);
        }
        {
            var Q0;
            {var subQ3=sQuery(id+"F4.wireOp",EDGE,"E264.right");Q0=makeQuery(id+"F4.imprint","IMPRINT",FACE,{"disambiguationData":[TD([[makeQuery(id+"F4.imprint","IMPRINT",EDGE,{"derivedFrom":subQ3}),-1.0]])]});}
            var Q1;
            {var subQ1=sQuery(id+"F4.wireOp",EDGE,"E268");Q1=makeQuery(id+"F4.imprint","IMPRINT",FACE,{"disambiguationData":[TD([[makeQuery(id+"F4.imprint","IMPRINT",EDGE,{"derivedFrom":subQ1}),-1.0]])]});}
            var Q2;
            {var subQ2=sQuery(id+"F4.wireOp",EDGE,"E269");Q2=makeQuery(id+"F4.imprint","IMPRINT",FACE,{"disambiguationData":[TD([[makeQuery(id+"F4.imprint","IMPRINT",EDGE,{"derivedFrom":subQ2}),1.0]])]});}
            var Q3;
            {var subQ0=sQuery(id+"F4.wireOp",EDGE,"E264.left");Q3=makeQuery(id+"F4.imprint","IMPRINT",FACE,{"disambiguationData":[TD([[makeQuery(id+"F4.imprint","IMPRINT",EDGE,{"derivedFrom":subQ0}),1.0]])]});}
            extrude(context, id + "F5", {"entities" : qUnion([Q0, Q1, Q2, Q3]), "operationType" : NewBodyOperationType.REMOVE, "depth" : 5 * mm});
        }
        {
            var Q0;
            Q0=makeQuery(id+"F0.imprint","IMPRINT",FACE,{"disambiguationData":[TD([[makeQuery(id+"F0.imprint","IMPRINT",EDGE,{"derivedFrom":sQuery(id+"F0.wireOp",EDGE,"E13.0")}),1.0]])]});
            extrude(context, id + "F6", {"entities" : qUnion([Q0]), "operationType" : NewBodyOperationType.ADD, "depth" : 3 * mm});
        }
    });
